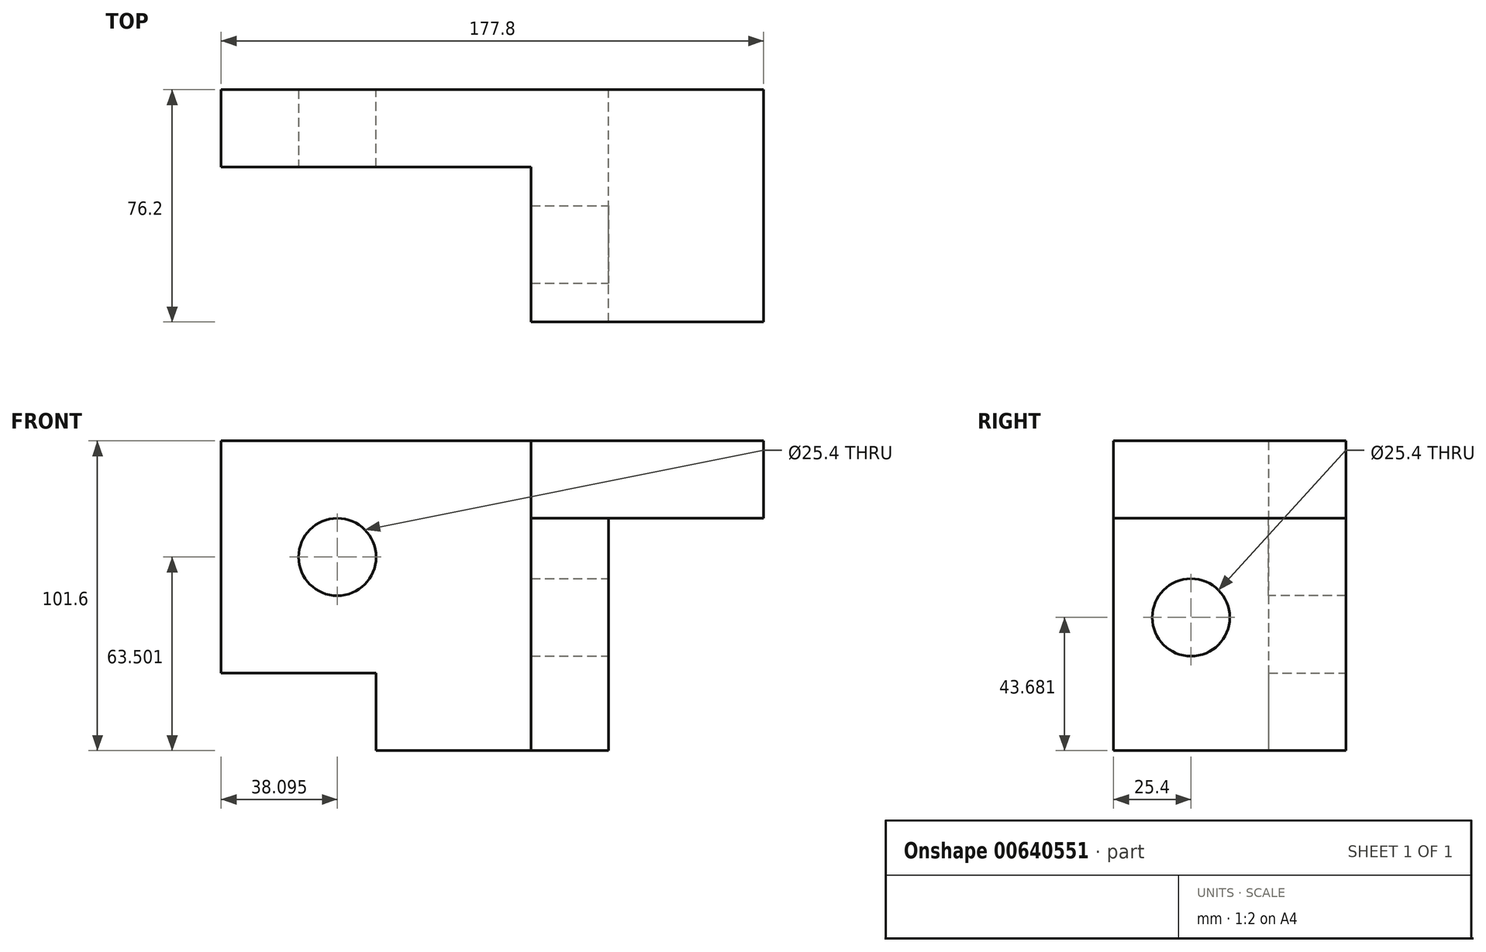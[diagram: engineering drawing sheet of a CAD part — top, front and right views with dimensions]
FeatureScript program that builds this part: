
annotation { "Feature Type Name" : "Feature", "Feature Type Description" : "" }
export const myFeature = defineFeature(function(context is Context, id is Id, definition is map)
    precondition{}
    {
        {
            var Q0;
            Q0=qCreatedBy(makeId("Front.planeOp"),FACE);
            var sketch = newSketch(context, id + "F0", { "sketchPlane" : qUnion([Q0])});
            skLineSegment(sketch, "E0.bottom", {"start": v(-22.9, 63.92) * mm, "end": v(53.3, 63.92) * mm});
            skLineSegment(sketch, "E0.top", {"start": v(-22.9, -37.68) * mm, "end": v(53.3, -37.68) * mm});
            skLineSegment(sketch, "E0.left", {"start": v(-22.9, 63.92) * mm, "end": v(-22.9, -37.68) * mm});
            skLineSegment(sketch, "E0.right", {"start": v(53.3, 63.92) * mm, "end": v(53.3, -37.68) * mm});
            skLineSegment(sketch, "E1.bottom", {"start": v(-22.9, 63.92) * mm, "end": v(-73.7, 63.92) * mm});
            skLineSegment(sketch, "E1.top", {"start": v(-22.9, -12.28) * mm, "end": v(-73.7, -12.28) * mm});
            skLineSegment(sketch, "E1.left", {"start": v(-22.9, 63.92) * mm, "end": v(-22.9, -12.28) * mm});
            skLineSegment(sketch, "E1.right", {"start": v(-73.7, 63.92) * mm, "end": v(-73.7, -12.28) * mm});
            skLineSegment(sketch, "E2.bottom", {"start": v(53.3, 63.92) * mm, "end": v(104.1, 63.92) * mm});
            skLineSegment(sketch, "E2.top", {"start": v(53.3, 38.52) * mm, "end": v(104.1, 38.52) * mm});
            skLineSegment(sketch, "E2.left", {"start": v(53.3, 63.92) * mm, "end": v(53.3, 38.52) * mm});
            skLineSegment(sketch, "E2.right", {"start": v(104.1, 63.92) * mm, "end": v(104.1, 38.52) * mm});
            skLineSegment(sketch, "E3", {"start": v(27.9, 63.92) * mm, "end": v(27.9, -37.68) * mm});
            skSolve(sketch);
        }
        {
            var Q0;
            Q0=makeQuery(id+"F0.imprint","IMPRINT",FACE,{"disambiguationData":[TD([[makeQuery(id+"F0.imprint","IMPRINT",EDGE,{"derivedFrom":sQuery(id+"F0.wireOp",EDGE,"E1.bottom")}),1.0]])]});
            var Q1;
            {var subQ1=sQuery(id+"F0.wireOp",EDGE,"E0.left");Q1=makeQuery(id+"F0.imprint","IMPRINT",FACE,{"disambiguationData":[TD([[makeQuery(id+"F0.imprint","IMPRINT",EDGE,{"derivedFrom":subQ1}),1.0]])]});}
            extrude(context, id + "F1", {"entities" : qUnion([Q0, Q1]), "depth" : 25.4 * mm, "offsetDistance" : 25.4 * mm});
        }
        {
            var Q0;
            {var subQ3=sQuery(id+"F0.wireOp",EDGE,"E0.right");Q0=makeQuery(id+"F0.imprint","IMPRINT",FACE,{"disambiguationData":[TD([[makeQuery(id+"F0.imprint","IMPRINT",EDGE,{"derivedFrom":subQ3}),-1.0]])]});}
            var Q1;
            Q1=makeQuery(id+"F0.imprint","IMPRINT",FACE,{"disambiguationData":[TD([[makeQuery(id+"F0.imprint","IMPRINT",EDGE,{"derivedFrom":sQuery(id+"F0.wireOp",EDGE,"E2.bottom")}),-1.0]])]});
            extrude(context, id + "F2", {"entities" : qUnion([Q0, Q1]), "operationType" : NewBodyOperationType.ADD, "depth" : 76.2 * mm, "offsetDistance" : 25.4 * mm});
        }
        {
            var Q0;
            Q0=makeQuery(id+"F2.opExtrude","SWEPT_FACE",FACE,{"disambiguationData":[OSD([sQuery(id+"F0.wireOp",EDGE,"E0.right")])]});
            var sketch = newSketch(context, id + "F3", { "sketchPlane" : qUnion([Q0])});
            skCircle(sketch, "E4", {"center": v(-50.8, 6) * mm, "radius": 12.7 * mm});
            skSolve(sketch);
        }
        {
            var Q0;
            Q0=makeQuery(id+"F1.opExtrude","CAP_FACE",FACE,{"disambiguationData":[OSD([sQuery(id+"F0.wireOp",EDGE,"E0.bottom"),sQuery(id+"F0.wireOp",EDGE,"E0.top"),sQuery(id+"F0.wireOp",EDGE,"E0.left"),sQuery(id+"F0.wireOp",EDGE,"E1.bottom"),sQuery(id+"F0.wireOp",EDGE,"E1.top"),sQuery(id+"F0.wireOp",EDGE,"E1.right"),sQuery(id+"F0.wireOp",EDGE,"E3")])],"isStart":false});
            var sketch = newSketch(context, id + "F4", { "sketchPlane" : qUnion([Q0])});
            skCircle(sketch, "E5", {"center": v(-35.6, 25.82) * mm, "radius": 12.7 * mm});
            skPoint(sketch, "E5.centerSnap0", {"position": v(-73.7, 25.82) * mm});
            skSolve(sketch);
        }
        {
            var Q0;
            Q0 = qSketchRegion(id + "F4", true);
            extrude(context, id + "F5", {"entities" : qUnion([Q0]), "operationType" : NewBodyOperationType.REMOVE, "oppositeDirection" : true, "depth" : 25.4 * mm, "offsetDistance" : 25.4 * mm});
        }
        {
            var Q0;
            Q0=makeQuery(id+"F3.imprint","IMPRINT",FACE,{"disambiguationData":[TD([[makeQuery(id+"F3.imprint","IMPRINT",EDGE,{"derivedFrom":sQuery(id+"F3.wireOp",EDGE,"E4")}),-1.0]])]});
            extrude(context, id + "F6", {"entities" : qUnion([Q0]), "oppositeDirection" : true, "depth" : 25.4 * mm, "offsetDistance" : 25.4 * mm});
        }
    });
